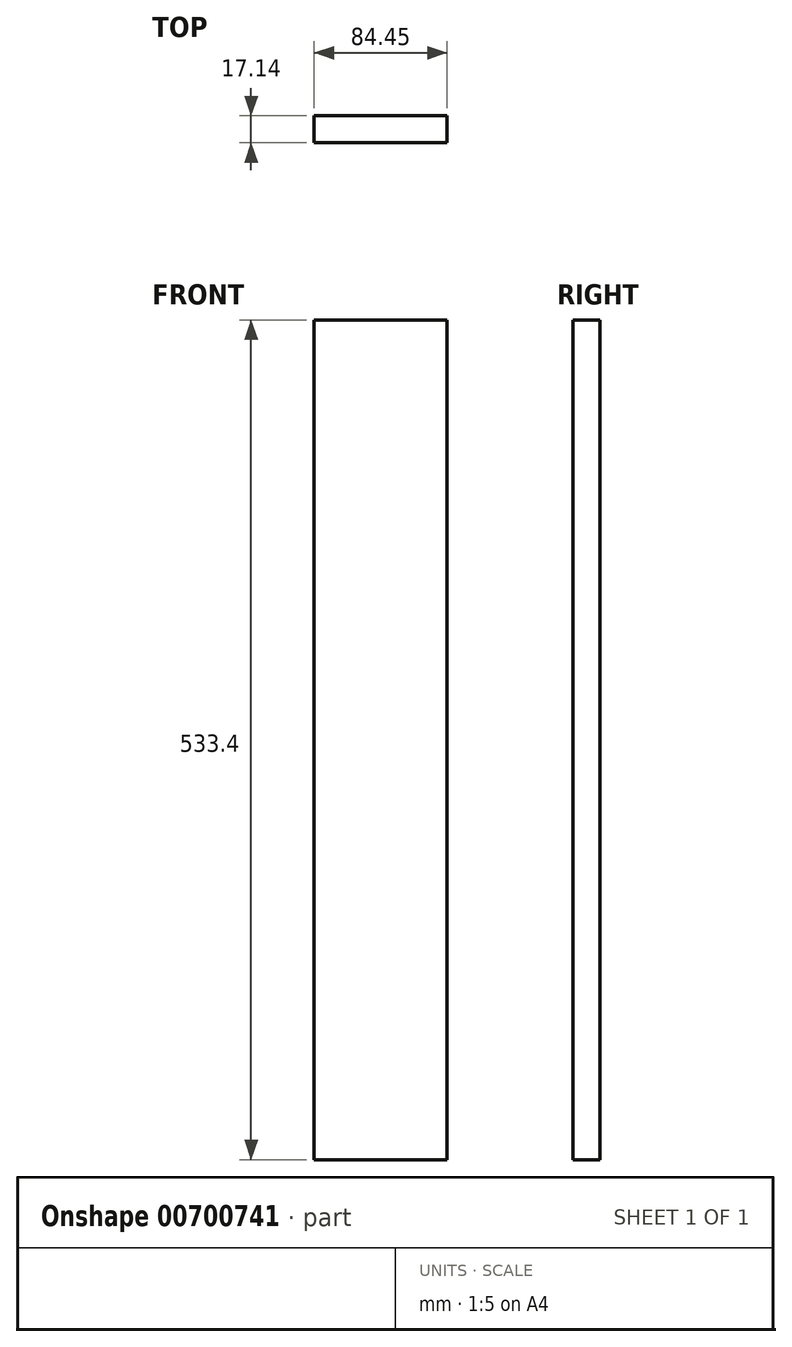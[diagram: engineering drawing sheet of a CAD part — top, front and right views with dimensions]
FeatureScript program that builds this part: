
annotation { "Feature Type Name" : "Feature", "Feature Type Description" : "" }
export const myFeature = defineFeature(function(context is Context, id is Id, definition is map)
    precondition{}
    {
        {
            var Q0;
            Q0=qCreatedBy(makeId("Front.planeOp"),FACE);
            var sketch = newSketch(context, id + "F0", { "sketchPlane" : qUnion([Q0])});
            skLineSegment(sketch, "E0.bottom", {"start": v(0, 0) * mm, "end": v(84.46, 0) * mm});
            skLineSegment(sketch, "E0.top", {"start": v(0, 533.4) * mm, "end": v(84.45, 533.4) * mm});
            skLineSegment(sketch, "E0.left", {"start": v(0, 0) * mm, "end": v(0, 533.4) * mm});
            skLineSegment(sketch, "E0.right", {"start": v(84.46, 0) * mm, "end": v(84.46, 533.4) * mm});
            skSolve(sketch);
        }
        {
            var Q0;
            Q0=makeQuery(id+"F0.imprint","IMPRINT",FACE,{"disambiguationData":[TD([[makeQuery(id+"F0.imprint","IMPRINT",EDGE,{"derivedFrom":sQuery(id+"F0.wireOp",EDGE,"E0.bottom")}),1.0]])]});
            extrude(context, id + "F1", {"entities" : qUnion([Q0]), "depth" : 17.14 * mm, "offsetDistance" : 25.4 * mm});
        }
    });
